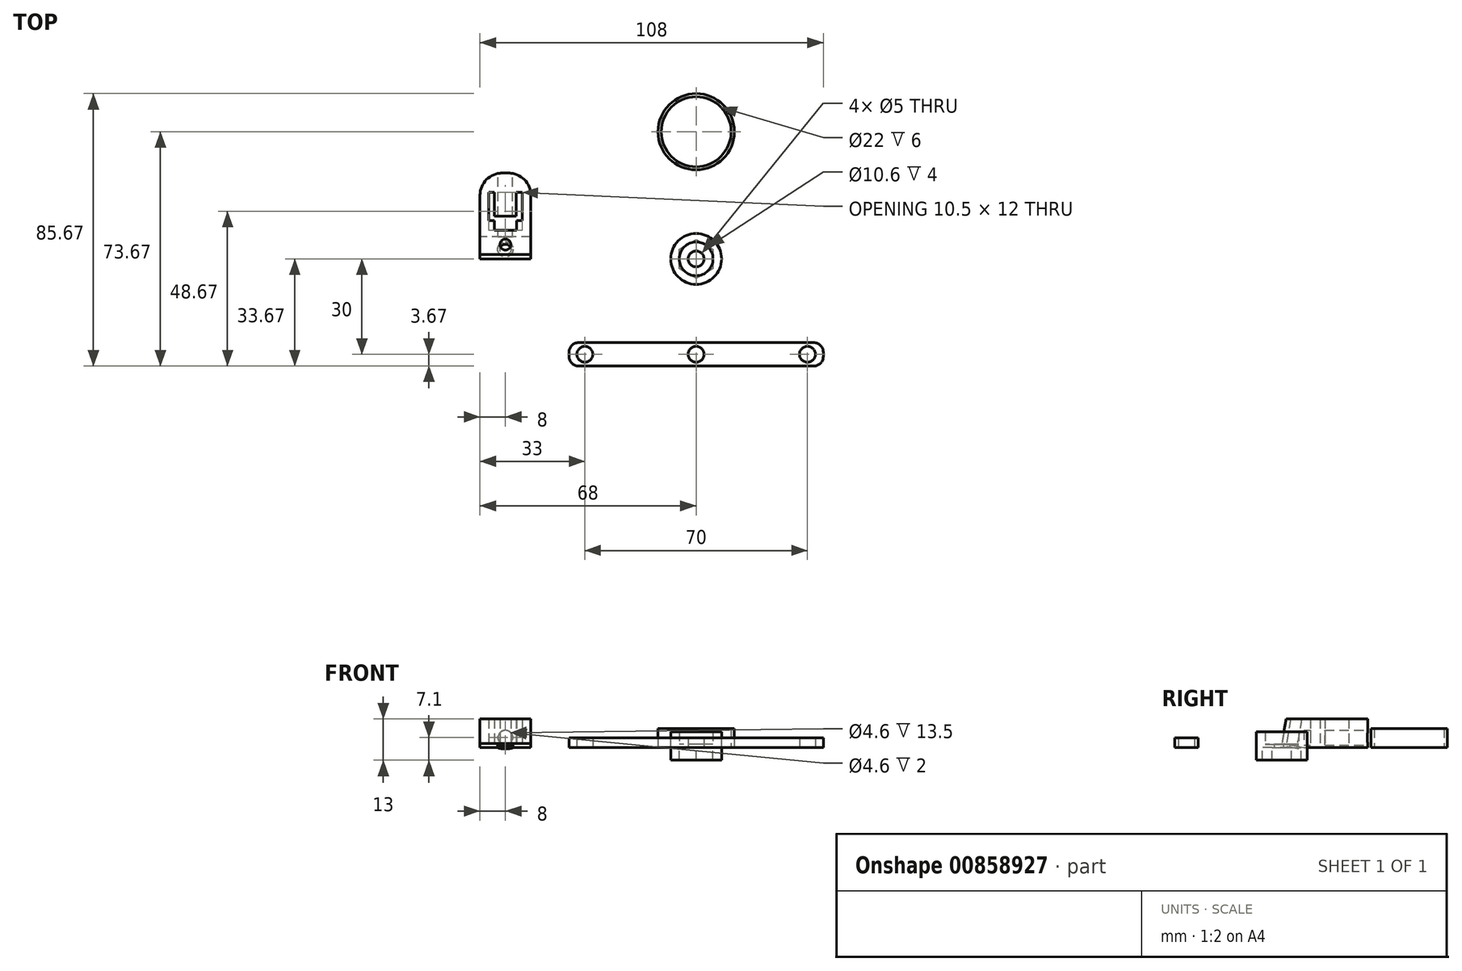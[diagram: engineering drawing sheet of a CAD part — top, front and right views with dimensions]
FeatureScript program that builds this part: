
annotation { "Feature Type Name" : "Feature", "Feature Type Description" : "" }
export const myFeature = defineFeature(function(context is Context, id is Id, definition is map)
    precondition{}
    {
        {
            var Q0;
            Q0=qCreatedBy(makeId("Top.planeOp"),FACE);
            var sketch = newSketch(context, id + "F0", { "sketchPlane" : qUnion([Q0])});
            skCircle(sketch, "E0.cCircle", {"center": v(0, 0) * mm, "radius": 5.3 * mm});
            skLineSegment(sketch, "E0.0", {"start": v(5.3, -3.06) * mm, "end": v(0, -6.12) * mm});
            skLineSegment(sketch, "E0.1", {"start": v(0, -6.12) * mm, "end": v(-5.3, -3.06) * mm});
            skLineSegment(sketch, "E0.2", {"start": v(-5.3, -3.06) * mm, "end": v(-5.3, 3.06) * mm});
            skLineSegment(sketch, "E0.3", {"start": v(-5.3, 3.06) * mm, "end": v(0, 6.12) * mm});
            skLineSegment(sketch, "E0.4", {"start": v(0, 6.12) * mm, "end": v(5.3, 3.06) * mm});
            skLineSegment(sketch, "E0.5", {"start": v(5.3, 3.06) * mm, "end": v(5.3, -3.06) * mm});
            skPoint(sketch, "E0.0.midPoint", {"position": v(2.65, -4.59) * mm});
            skCircle(sketch, "E1", {"center": v(0, 0) * mm, "radius": 8 * mm});
            skCircle(sketch, "E2", {"center": v(0, 0) * mm, "radius": 2.5 * mm});
            skPoint(sketch, "E3", {"position": v(0, -30) * mm});
            skLineSegment(sketch, "E4.bottom", {"start": v(37, -33.68) * mm, "end": v(-37, -33.67) * mm});
            skLineSegment(sketch, "E4.top", {"start": v(37, -26.33) * mm, "end": v(-37, -26.32) * mm});
            skLineSegment(sketch, "E4.left", {"start": v(40, -30.68) * mm, "end": v(40, -29.32) * mm});
            skLineSegment(sketch, "E4.right", {"start": v(-40, -30.67) * mm, "end": v(-40, -29.32) * mm});
            skPoint(sketch, "E5", {"position": v(35, -30) * mm});
            skPoint(sketch, "E6", {"position": v(-35, -30) * mm});
            skCircle(sketch, "E7", {"center": v(-35, -30) * mm, "radius": 2.5 * mm});
            skCircle(sketch, "E8", {"center": v(0, -30) * mm, "radius": 2.5 * mm});
            skCircle(sketch, "E9", {"center": v(35, -30) * mm, "radius": 2.5 * mm});
            skPoint(sketch, "E10.visualSharp", {"position": v(-40, -26.32) * mm});
            skArc(sketch, "E10.filletArc", {"start": v(-37, -26.32) * mm, "mid": v(-39.12, -27.2) * mm, "end": v(-40, -29.32) * mm});
            skPoint(sketch, "E11.visualSharp", {"position": v(-40, -33.67) * mm});
            skArc(sketch, "E11.filletArc", {"start": v(-40, -30.67) * mm, "mid": v(-39.12, -32.8) * mm, "end": v(-37, -33.67) * mm});
            skPoint(sketch, "E12.visualSharp", {"position": v(40, -33.68) * mm});
            skArc(sketch, "E12.filletArc", {"start": v(37, -33.68) * mm, "mid": v(39.12, -32.8) * mm, "end": v(40, -30.68) * mm});
            skPoint(sketch, "E13.visualSharp", {"position": v(40, -26.33) * mm});
            skArc(sketch, "E13.filletArc", {"start": v(40, -29.32) * mm, "mid": v(39.12, -27.2) * mm, "end": v(37, -26.32) * mm});
            skPoint(sketch, "E14", {"position": v(0, 40) * mm});
            skCircle(sketch, "E15", {"center": v(0, 40) * mm, "radius": 11 * mm});
            skCircle(sketch, "E16", {"center": v(0, 40) * mm, "radius": 12 * mm});
            skLineSegment(sketch, "E17.bottom", {"start": v(-52, 0) * mm, "end": v(-68, 0) * mm});
            skLineSegment(sketch, "E17.top", {"start": v(-52, 27) * mm, "end": v(-68, 27) * mm});
            skLineSegment(sketch, "E17.left", {"start": v(-52, 0) * mm, "end": v(-52, 27) * mm});
            skLineSegment(sketch, "E17.right", {"start": v(-68, 0) * mm, "end": v(-68, 27) * mm});
            skLineSegment(sketch, "E18", {"start": v(-65.25, 21) * mm, "end": v(-65.25, 12) * mm});
            skLineSegment(sketch, "E19", {"start": v(-65.25, 12) * mm, "end": v(-54.75, 12) * mm});
            skLineSegment(sketch, "E20", {"start": v(-54.75, 12) * mm, "end": v(-54.75, 21) * mm});
            skLineSegment(sketch, "E21", {"start": v(-54.75, 21) * mm, "end": v(-56.55, 21) * mm});
            skLineSegment(sketch, "E22", {"start": v(-56.55, 21) * mm, "end": v(-56.55, 13.5) * mm});
            skLineSegment(sketch, "E23", {"start": v(-56.55, 13.5) * mm, "end": v(-63.45, 13.5) * mm});
            skLineSegment(sketch, "E24", {"start": v(-63.45, 13.5) * mm, "end": v(-63.45, 21) * mm});
            skLineSegment(sketch, "E25", {"start": v(-63.45, 21) * mm, "end": v(-65.25, 21) * mm});
            skPoint(sketch, "E26", {"position": v(-60, 12) * mm});
            skPoint(sketch, "E27", {"position": v(-60, 0) * mm});
            skLineSegment(sketch, "E28", {"start": v(-68, 7) * mm, "end": v(-52, 7) * mm});
            skLineSegment(sketch, "E29", {"start": v(-63.5, 12) * mm, "end": v(-63.5, 9) * mm});
            skLineSegment(sketch, "E30", {"start": v(-63.5, 9) * mm, "end": v(-56.5, 9) * mm});
            skLineSegment(sketch, "E31", {"start": v(-56.5, 9) * mm, "end": v(-56.5, 12) * mm});
            skPoint(sketch, "E32", {"position": v(-60, 9) * mm});
            skSolve(sketch);
        }
        {
            var Q0;
            Q0=makeQuery(id+"F0.imprint","IMPRINT",FACE,{"disambiguationData":[TD([[makeQuery(id+"F0.imprint","IMPRINT",EDGE,{"derivedFrom":sQuery(id+"F0.wireOp",EDGE,"E0.0")}),1.0]])]});
            extrude(context, id + "F1", {"entities" : qUnion([Q0]), "oppositeDirection" : true, "depth" : 4 * mm, "offsetDistance" : 25 * mm});
        }
        {
            var Q0;
            Q0=makeQuery(id+"F0.imprint","IMPRINT",FACE,{"disambiguationData":[TD([[makeQuery(id+"F0.imprint","IMPRINT",EDGE,{"derivedFrom":sQuery(id+"F0.wireOp",EDGE,"E1")}),1.0]])]});
            var Q1;
            {var subQ0=sQuery(id+"F0.wireOp",EDGE,"E0.1");var subQ1=sQuery(id+"F0.wireOp",EDGE,"E0.cCircle");var subQ2=makeQuery(id+"F0.imprint","INTERSECT",VERTEX,{"derivedFrom":[subQ1,subQ0]});Q1=makeQuery(id+"F0.imprint","IMPRINT",FACE,{"disambiguationData":[TD([[makeQuery(id+"F0.imprint","IMPRINT",EDGE,{"disambiguationData":[TD([[subQ2,-1.0]])],"derivedFrom":subQ1}),-1.0]])]});}
            var Q2;
            {var subQ0=sQuery(id+"F0.wireOp",EDGE,"E0.1");var subQ1=sQuery(id+"F0.wireOp",EDGE,"E0.cCircle");var subQ2=makeQuery(id+"F0.imprint","INTERSECT",VERTEX,{"derivedFrom":[subQ1,subQ0]});Q2=makeQuery(id+"F0.imprint","IMPRINT",FACE,{"disambiguationData":[TD([[makeQuery(id+"F0.imprint","IMPRINT",EDGE,{"disambiguationData":[TD([[subQ2,1.0]])],"derivedFrom":subQ1}),-1.0]])]});}
            var Q3;
            {var subQ0=sQuery(id+"F0.wireOp",EDGE,"E0.3");var subQ1=sQuery(id+"F0.wireOp",EDGE,"E0.cCircle");var subQ2=makeQuery(id+"F0.imprint","INTERSECT",VERTEX,{"derivedFrom":[subQ1,subQ0]});Q3=makeQuery(id+"F0.imprint","IMPRINT",FACE,{"disambiguationData":[TD([[makeQuery(id+"F0.imprint","IMPRINT",EDGE,{"disambiguationData":[TD([[subQ2,-1.0]])],"derivedFrom":subQ1}),-1.0]])]});}
            var Q4;
            {var subQ0=sQuery(id+"F0.wireOp",EDGE,"E0.5");var subQ1=sQuery(id+"F0.wireOp",EDGE,"E0.cCircle");var subQ2=makeQuery(id+"F0.imprint","INTERSECT",VERTEX,{"derivedFrom":[subQ1,subQ0]});Q4=makeQuery(id+"F0.imprint","IMPRINT",FACE,{"disambiguationData":[TD([[makeQuery(id+"F0.imprint","IMPRINT",EDGE,{"disambiguationData":[TD([[subQ2,1.0]])],"derivedFrom":subQ1}),-1.0]])]});}
            var Q5;
            {var subQ0=sQuery(id+"F0.wireOp",EDGE,"E0.5");var subQ1=sQuery(id+"F0.wireOp",EDGE,"E0.cCircle");var subQ2=makeQuery(id+"F0.imprint","INTERSECT",VERTEX,{"derivedFrom":[subQ1,subQ0]});Q5=makeQuery(id+"F0.imprint","IMPRINT",FACE,{"disambiguationData":[TD([[makeQuery(id+"F0.imprint","IMPRINT",EDGE,{"disambiguationData":[TD([[subQ2,-1.0]])],"derivedFrom":subQ1}),-1.0]])]});}
            var Q6;
            {var subQ0=sQuery(id+"F0.wireOp",EDGE,"E0.4");var subQ1=sQuery(id+"F0.wireOp",EDGE,"E0.cCircle");var subQ2=makeQuery(id+"F0.imprint","INTERSECT",VERTEX,{"derivedFrom":[subQ1,subQ0]});Q6=makeQuery(id+"F0.imprint","IMPRINT",FACE,{"disambiguationData":[TD([[makeQuery(id+"F0.imprint","IMPRINT",EDGE,{"disambiguationData":[TD([[subQ2,-1.0]])],"derivedFrom":subQ1}),-1.0]])]});}
            extrude(context, id + "F2", {"entities" : qUnion([Q0, Q1, Q2, Q3, Q4, Q5, Q6]), "operationType" : NewBodyOperationType.ADD, "depth" : 5 * mm, "offsetDistance" : 25 * mm});
        }
        {
            var Q0;
            Q0=makeQuery(id+"F0.imprint","IMPRINT",FACE,{"disambiguationData":[TD([[makeQuery(id+"F0.imprint","IMPRINT",EDGE,{"derivedFrom":sQuery(id+"F0.wireOp",EDGE,"E2")}),-1.0]])]});
            extrude(context, id + "F3", {"entities" : qUnion([Q0]), "operationType" : NewBodyOperationType.ADD, "depth" : 1 * mm, "offsetDistance" : 25 * mm});
        }
        {
            var Q0;
            Q0=makeQuery(id+"F0.imprint","IMPRINT",FACE,{"disambiguationData":[TD([[makeQuery(id+"F0.imprint","IMPRINT",EDGE,{"derivedFrom":sQuery(id+"F0.wireOp",EDGE,"E4.bottom")}),-1.0]])]});
            extrude(context, id + "F4", {"entities" : qUnion([Q0]), "depth" : 3 * mm, "offsetDistance" : 25 * mm});
        }
        {
            var Q0;
            Q0=makeQuery(id+"F0.imprint","IMPRINT",FACE,{"disambiguationData":[TD([[makeQuery(id+"F0.imprint","IMPRINT",EDGE,{"derivedFrom":sQuery(id+"F0.wireOp",EDGE,"E15")}),-1.0]])]});
            extrude(context, id + "F5", {"entities" : qUnion([Q0]), "depth" : 6 * mm, "offsetDistance" : 25 * mm});
        }
        {
            var Q0;
            Q0=makeQuery(id+"F0.imprint","IMPRINT",FACE,{"disambiguationData":[TD([[makeQuery(id+"F0.imprint","IMPRINT",EDGE,{"derivedFrom":sQuery(id+"F0.wireOp",EDGE,"E17.bottom")}),-1.0]])]});
            var Q1;
            {var subQ0=sQuery(id+"F0.wireOp",EDGE,"E17.top");Q1=makeQuery(id+"F0.imprint","IMPRINT",FACE,{"disambiguationData":[TD([[makeQuery(id+"F0.imprint","IMPRINT",EDGE,{"derivedFrom":subQ0}),1.0]])]});}
            extrude(context, id + "F6", {"entities" : qUnion([Q0, Q1]), "depth" : 9 * mm, "offsetDistance" : 25 * mm});
        }
        {
            var Q0;
            Q0=sQuery(id+"F0.wireOp",EDGE,"E28");
            cPlane(context, id + "F7", {"entities" : qUnion([Q0]), "cplaneType" : CPlaneType.LINE_ANGLE, "offset" : 25 * mm, "angle" : 100 * degree, "oppositeDirection" : true, "width" : 150 * mm, "height" : 150 * mm});
        }
        {
            var Q0;
            Q0=qCreatedBy(id+"F7.planeOp",FACE);
            var sketch = newSketch(context, id + "F8", { "sketchPlane" : qUnion([Q0])});
            skLineSegment(sketch, "E33", {"start": v(-52, -6.9) * mm, "end": v(-68, -6.9) * mm});
            skLineSegment(sketch, "E34", {"start": v(-52, 0.21) * mm, "end": v(-68, 0.21) * mm});
            skLineSegment(sketch, "E35", {"start": v(-52, 0.21) * mm, "end": v(-52, -6.9) * mm});
            skLineSegment(sketch, "E36", {"start": v(-68, 0.21) * mm, "end": v(-68, -6.9) * mm});
            skPoint(sketch, "E37", {"position": v(-60, -2.9) * mm});
            skPoint(sketch, "E37.positionSnap0", {"position": v(-60, -6.9) * mm});
            skCircle(sketch, "E38", {"center": v(-60, -2.9) * mm, "radius": 1.7 * mm});
            skCircle(sketch, "E39", {"center": v(-60, -2.9) * mm, "radius": 2.4 * mm});
            skLineSegment(sketch, "E40.0", {"start": v(-52, 1.56) * mm, "end": v(-68, 1.56) * mm});
            skLineSegment(sketch, "E41", {"start": v(-68, 0.21) * mm, "end": v(-68, 1.56) * mm});
            skLineSegment(sketch, "E42", {"start": v(-52, 0.21) * mm, "end": v(-52, 1.56) * mm});
            skSolve(sketch);
        }
        {
            var Q0;
            Q0=makeQuery(id+"F8.imprint","IMPRINT",FACE,{"disambiguationData":[TD([[makeQuery(id+"F8.imprint","IMPRINT",EDGE,{"derivedFrom":sQuery(id+"F8.wireOp",EDGE,"E33")}),-1.0]])]});
            var Q1;
            Q1=makeQuery(id+"F8.imprint","IMPRINT",FACE,{"disambiguationData":[TD([[makeQuery(id+"F8.imprint","IMPRINT",EDGE,{"derivedFrom":sQuery(id+"F8.wireOp",EDGE,"E38")}),-1.0]])]});
            var Q2;
            Q2=makeQuery(id+"F8.imprint","IMPRINT",FACE,{"disambiguationData":[TD([[makeQuery(id+"F8.imprint","IMPRINT",EDGE,{"derivedFrom":sQuery(id+"F8.wireOp",EDGE,"E38")}),1.0]])]});
            extrude(context, id + "F9", {"entities" : qUnion([Q0, Q1, Q2]), "operationType" : NewBodyOperationType.REMOVE, "endBound" : BoundingType.THROUGH_ALL, "depth" : 25 * mm, "offsetDistance" : 25 * mm});
        }
        {
            var Q0;
            Q0=makeQuery(id+"F8.imprint","IMPRINT",FACE,{"disambiguationData":[TD([[makeQuery(id+"F8.imprint","IMPRINT",EDGE,{"derivedFrom":sQuery(id+"F8.wireOp",EDGE,"E38")}),1.0]])]});
            extrude(context, id + "F10", {"entities" : qUnion([Q0]), "operationType" : NewBodyOperationType.REMOVE, "endBound" : BoundingType.THROUGH_ALL, "oppositeDirection" : true, "depth" : 25 * mm, "offsetDistance" : 25 * mm});
        }
        {
            var Q0;
            Q0=makeQuery(id+"F8.imprint","IMPRINT",FACE,{"disambiguationData":[TD([[makeQuery(id+"F8.imprint","IMPRINT",EDGE,{"derivedFrom":sQuery(id+"F8.wireOp",EDGE,"E38")}),-1.0]])]});
            extrude(context, id + "F11", {"entities" : qUnion([Q0]), "operationType" : NewBodyOperationType.ADD, "depth" : 0.7 * mm, "offsetDistance" : 25 * mm});
        }
        {
            var Q0;
            Q0=makeQuery(id+"F6.opExtrude","SWEPT_FACE",FACE,{"disambiguationData":[OSD([sQuery(id+"F0.wireOp",EDGE,"E17.top")])]});
            var sketch = newSketch(context, id + "F12", { "sketchPlane" : qUnion([Q0])});
            skPoint(sketch, "E43.0", {"position": v(60, 0.7) * mm});
            skPoint(sketch, "E44", {"position": v(60, 3.1) * mm});
            skCircle(sketch, "E45", {"center": v(60, 3.1) * mm, "radius": 2.3 * mm});
            skSolve(sketch);
        }
        {
            var Q0;
            Q0=makeQuery(id+"F12.imprint","IMPRINT",FACE,{"disambiguationData":[TD([[makeQuery(id+"F12.imprint","IMPRINT",EDGE,{"derivedFrom":sQuery(id+"F12.wireOp",EDGE,"E45")}),1.0]])]});
            extrude(context, id + "F13", {"entities" : qUnion([Q0]), "operationType" : NewBodyOperationType.REMOVE, "oppositeDirection" : true, "depth" : 20 * mm, "offsetDistance" : 25 * mm});
        }
        {
            var Q0;
            Q0=makeQuery(id+"F8.imprint","IMPRINT",FACE,{"disambiguationData":[TD([[makeQuery(id+"F8.imprint","IMPRINT",EDGE,{"derivedFrom":sQuery(id+"F8.wireOp",EDGE,"E34")}),-1.0]])]});
            extrude(context, id + "F14", {"entities" : qUnion([Q0]), "operationType" : NewBodyOperationType.REMOVE, "endBound" : BoundingType.THROUGH_ALL, "oppositeDirection" : true, "depth" : 25 * mm, "offsetDistance" : 25 * mm});
        }
        {
            var Q0;
            Q0=makeQuery(id+"F6.opExtrude","SWEPT_EDGE",EDGE,{"disambiguationData":[OSD([sQuery(id+"F0.wireOp",EDGE,"E17.top"),sQuery(id+"F0.wireOp",EDGE,"E17.left")])]});
            var Q1;
            Q1=makeQuery(id+"F6.opExtrude","SWEPT_EDGE",EDGE,{"disambiguationData":[OSD([sQuery(id+"F0.wireOp",EDGE,"E17.top"),sQuery(id+"F0.wireOp",EDGE,"E17.right")])]});
            var Q2;
            Q2=makeQuery(id+"F14.boolean.opBoolean","COPY",EDGE,{"derivedFrom":makeQuery(id+"F14.opExtrude","SWEPT_EDGE",EDGE,{"disambiguationData":[OSD([sQuery(id+"F8.wireOp",EDGE,"E34"),sQuery(id+"F8.wireOp",EDGE,"E35"),sQuery(id+"F8.wireOp",EDGE,"E42")])]})});
            var Q3;
            Q3=makeQuery(id+"F14.boolean.opBoolean","COPY",EDGE,{"derivedFrom":makeQuery(id+"F14.opExtrude","SWEPT_EDGE",EDGE,{"disambiguationData":[OSD([sQuery(id+"F8.wireOp",EDGE,"E34"),sQuery(id+"F8.wireOp",EDGE,"E36"),sQuery(id+"F8.wireOp",EDGE,"E41")])]})});
            fillet(context, id + "F15", {"entities" : qUnion([Q0, Q1, Q2, Q3]), "tangentPropagation" : true, "radius" : 7 * mm, "defaultsChanged" : true, "vertexSettings" : [], "allowEdgeOverflow" : false});
        }
    });
